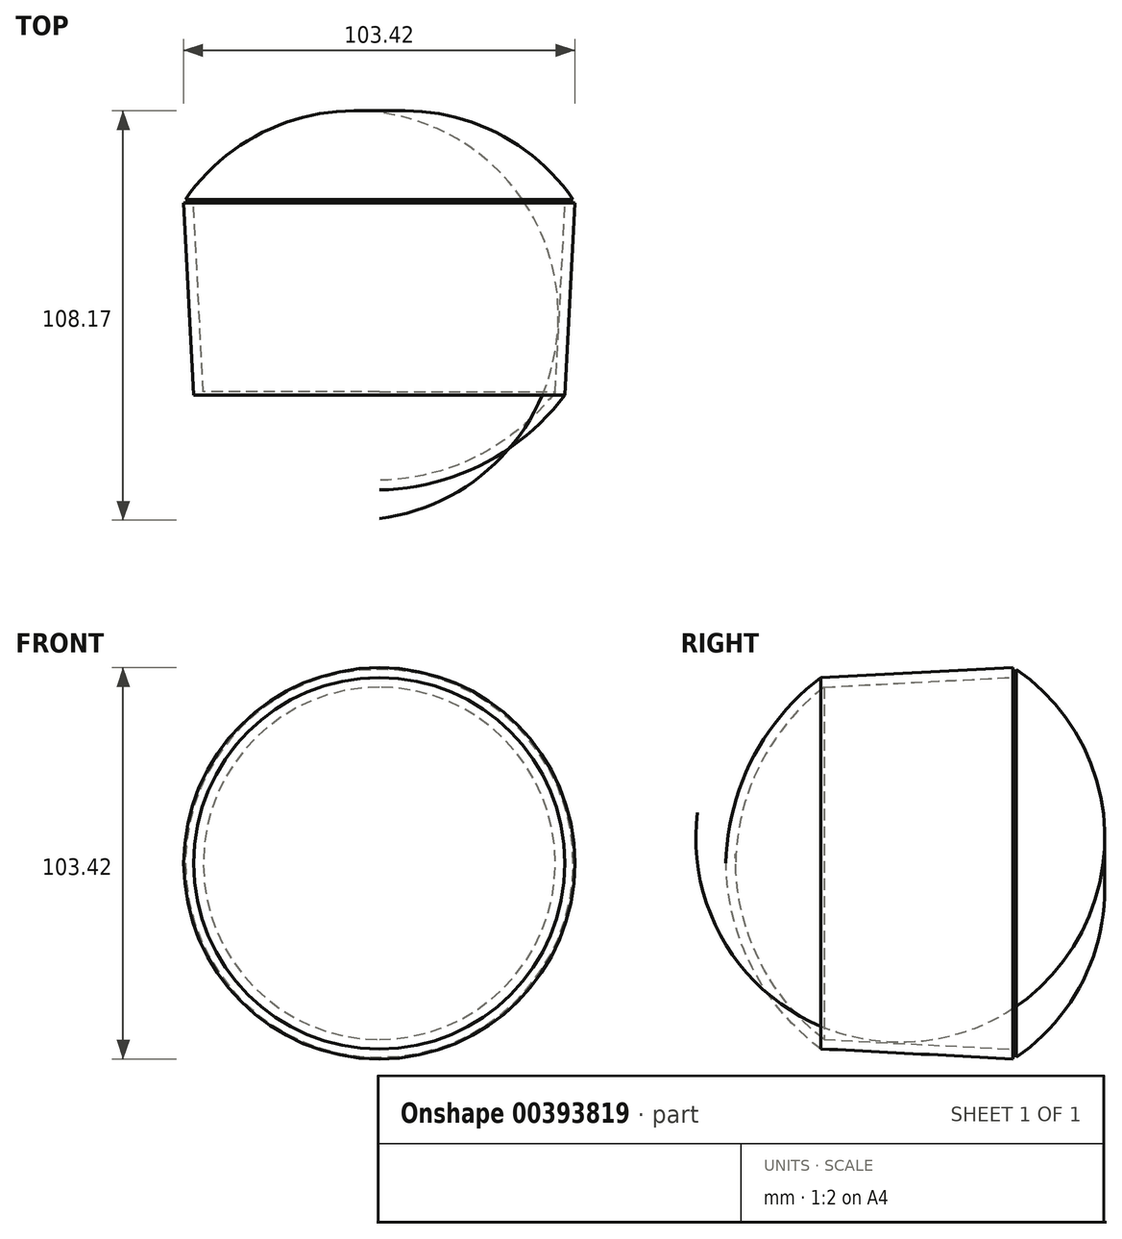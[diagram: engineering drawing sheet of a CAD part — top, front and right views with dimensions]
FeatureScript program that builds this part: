
annotation { "Feature Type Name" : "Feature", "Feature Type Description" : "" }
export const myFeature = defineFeature(function(context is Context, id is Id, definition is map)
    precondition{}
    {
        {
            var Q0;
            Q0=qCreatedBy(makeId("Front.planeOp"),FACE);
            var sketch = newSketch(context, id + "F0", { "sketchPlane" : qUnion([Q0])});
            skCircle(sketch, "E0", {"center": v(0, 0) * mm, "radius": 49.05 * mm});
            skSolve(sketch);
        }
        {
            var Q0;
            Q0=makeQuery(id+"F0.imprint","IMPRINT",FACE,{"disambiguationData":[TD([[makeQuery(id+"F0.imprint","IMPRINT",EDGE,{"derivedFrom":sQuery(id+"F0.wireOp",EDGE,"E0")}),1.0]])]});
            extrude(context, id + "F1", {"entities" : qUnion([Q0]), "oppositeDirection" : true, "depth" : 50.8 * mm, "hasDraft" : true, "draftAngle" : 3 * degree});
        }
        {
            var Q0;
            Q0=qCreatedBy(makeId("Top.planeOp"),FACE);
            var sketch = newSketch(context, id + "F2", { "sketchPlane" : qUnion([Q0])});
            skLineSegment(sketch, "E1", {"start": v(0, 0) * mm, "end": v(0, -24.67) * mm});
            skArc(sketch, "E2", {"start": v(-48.67, 0) * mm, "mid": v(-27.38, -18.34) * mm, "end": v(0, -24.67) * mm});
            skArc(sketch, "E3", {"start": v(0, -24.67) * mm, "mid": v(27.63, -18.83) * mm, "end": v(48.67, 0) * mm});
            skSolve(sketch);
        }
        {
            var Q0;
            Q0=qCreatedBy(makeId("Top.planeOp"),FACE);
            var sketch = newSketch(context, id + "F3", { "sketchPlane" : qUnion([Q0])});
            skLineSegment(sketch, "E4", {"start": v(0, 0) * mm, "end": v(0, -25.11) * mm});
            skArc(sketch, "E5", {"start": v(-49.12, 0) * mm, "mid": v(-27.45, -18.22) * mm, "end": v(0, -25.11) * mm});
            skLineSegment(sketch, "E6", {"start": v(-49.12, 0) * mm, "end": v(0, 0) * mm});
            skSolve(sketch);
        }
        {
            var Q0;
            Q0=makeQuery(id+"F3.imprint","IMPRINT",FACE,{"disambiguationData":[TD([[makeQuery(id+"F3.imprint","IMPRINT",EDGE,{"derivedFrom":sQuery(id+"F3.wireOp",EDGE,"E4")}),-1.0]])]});
            var Q1;
            Q1=sQuery(id+"F3.wireOp",EDGE,"E4");
            revolve(context, id + "F4", {"operationType" : NewBodyOperationType.ADD, "entities" : qUnion([Q0]), "axis" : qUnion([Q1]), "revolveType" : RevolveType.FULL});
        }
        {
            var Q0;
            Q0=makeQuery(id+"F1.opExtrude","CAP_FACE",FACE,{"disambiguationData":[OSD([sQuery(id+"F0.wireOp",EDGE,"E0")])],"isStart":false});
            shell(context, id + "F5", {"entities" : qUnion([Q0]), "thickness" : 2.54 * mm});
        }
        {
            var Q0;
            Q0=qCreatedBy(makeId("Top.planeOp"),FACE);
            var sketch = newSketch(context, id + "F6", { "sketchPlane" : qUnion([Q0])});
            skLineSegment(sketch, "E7", {"start": v(0, 74.67) * mm, "end": v(0, 51.06) * mm});
            skArc(sketch, "E8", {"start": v(0, 74.67) * mm, "mid": v(-28.87, 70.35) * mm, "end": v(-51.28, 51.66) * mm});
            skLineSegment(sketch, "E9", {"start": v(0, 51.06) * mm, "end": v(-51.28, 51.66) * mm});
            skSolve(sketch);
        }
        {
            var Q0;
            Q0=makeQuery(id+"F6.imprint","IMPRINT",FACE,{"disambiguationData":[TD([[makeQuery(id+"F6.imprint","IMPRINT",EDGE,{"derivedFrom":sQuery(id+"F6.wireOp",EDGE,"E7")}),-1.0]])]});
            var Q1;
            Q1=sQuery(id+"F2.wireOp",EDGE,"E1");
            revolve(context, id + "F7", {"entities" : qUnion([Q0]), "axis" : qUnion([Q1]), "revolveType" : RevolveType.FULL});
        }
    });
